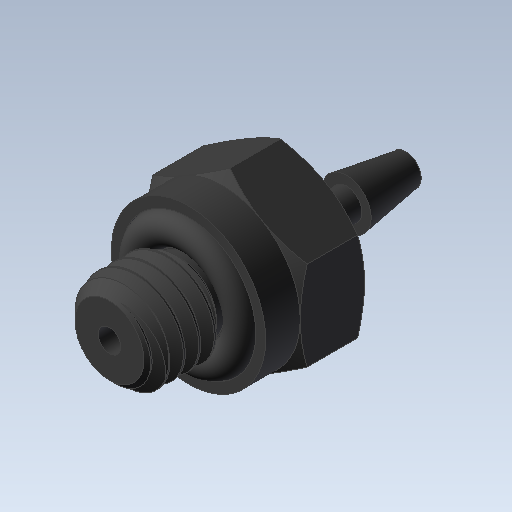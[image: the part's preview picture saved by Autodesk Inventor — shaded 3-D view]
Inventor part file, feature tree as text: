
AUTODESK INVENTOR PART (.ipt)
format: ipt  version: 2021.2 (Build 252289000, 289)  size: 416,256 bytes
history: native  units: in
note: dims shown in document units (in); Inventor stores cm internally (conversion verified against a paired STEP export)
features: revolve x2
ambient origin geometry x8: Origin, YZ Plane, XZ Plane, XY Plane, X Axis, Y Axis, Z Axis, Center Point
bodies: Solid1 (feature_tree), Solid2 (feature_tree)
feature tree (2):
  revolve  "Revolve2"  [1 undecoded]
  revolve  "Revolve3"  [1 undecoded]
note: 2 required parameter values undecoded (feature->parameter linkage not recoverable at this tier; creation-order binding heuristic only, values carry confidence <= 0.55)
